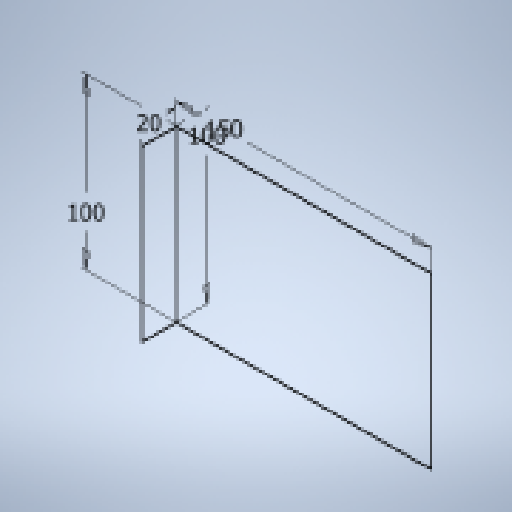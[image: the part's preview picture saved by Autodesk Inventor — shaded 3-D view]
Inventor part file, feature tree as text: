
AUTODESK INVENTOR PART (.ipt)
format: ipt  version: 2023 (Build 270158000, 158)  size: 131,072 bytes
history: native  units: mm
features: sketch x2
ambient origin geometry x8: Origin, YZ Plane, XZ Plane, XY Plane, X Axis, Y Axis, Z Axis, Center Point
feature tree (2):
  sketch  "Sketch1"  dims[d0=90.0mm]
  sketch  "Sketch2"  dims[d1=20.0mm d2=90.0mm d3=150.0mm]
